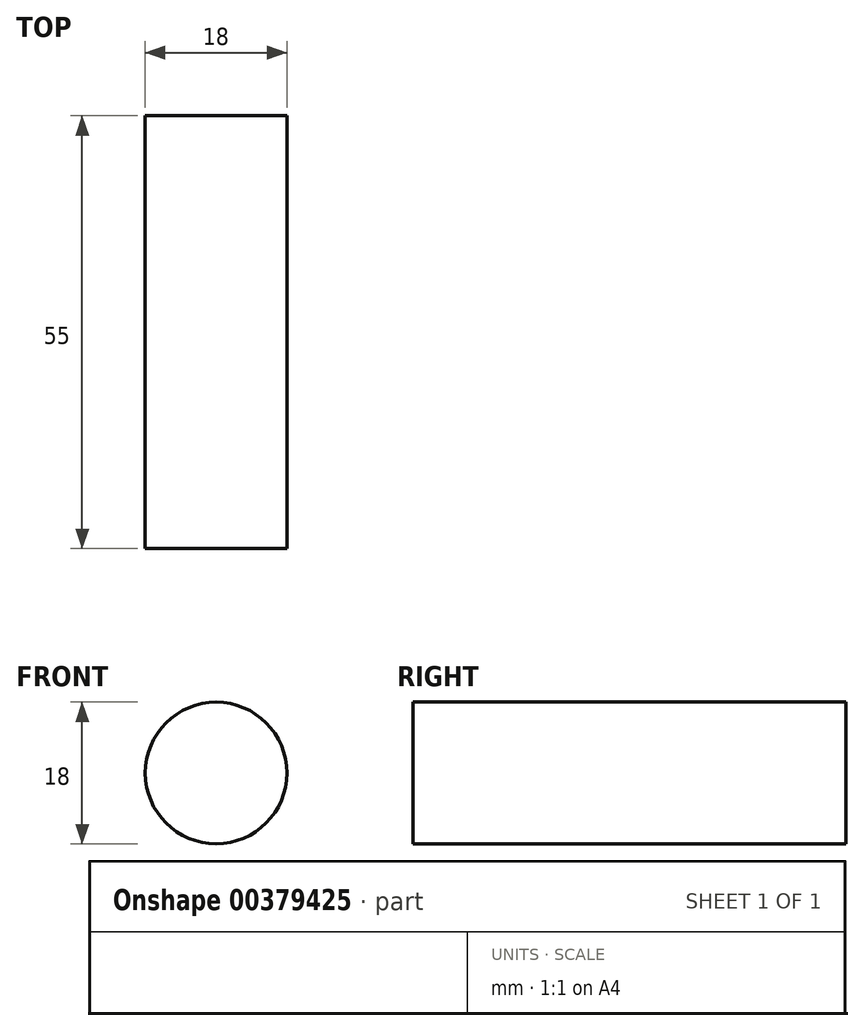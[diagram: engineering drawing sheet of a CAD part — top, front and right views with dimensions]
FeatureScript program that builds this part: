
annotation { "Feature Type Name" : "Feature", "Feature Type Description" : "" }
export const myFeature = defineFeature(function(context is Context, id is Id, definition is map)
    precondition{}
    {
        {
            var Q0;
            Q0=qCreatedBy(makeId("Right.planeOp"),FACE);
            var sketch = newSketch(context, id + "F0", { "sketchPlane" : qUnion([Q0])});
            skLineSegment(sketch, "E0.bottom", {"start": v(-39.58, 16.4) * mm, "end": v(15.42, 16.4) * mm});
            skLineSegment(sketch, "E0.top", {"start": v(-39.58, 7.4) * mm, "end": v(15.42, 7.4) * mm});
            skLineSegment(sketch, "E0.left", {"start": v(-39.58, 16.4) * mm, "end": v(-39.58, 7.4) * mm});
            skLineSegment(sketch, "E0.right", {"start": v(15.42, 16.4) * mm, "end": v(15.42, 7.4) * mm});
            skSolve(sketch);
        }
        {
            var Q0;
            Q0=makeQuery(id+"F0.imprint","IMPRINT",FACE,{"disambiguationData":[TD([[makeQuery(id+"F0.imprint","IMPRINT",EDGE,{"derivedFrom":sQuery(id+"F0.wireOp",EDGE,"E0.bottom")}),-1.0]])]});
            var Q1;
            Q1=sQuery(id+"F0.wireOp",EDGE,"E0.top");
            revolve(context, id + "F1", {"entities" : qUnion([Q0]), "axis" : qUnion([Q1]), "revolveType" : RevolveType.FULL});
        }
    });
